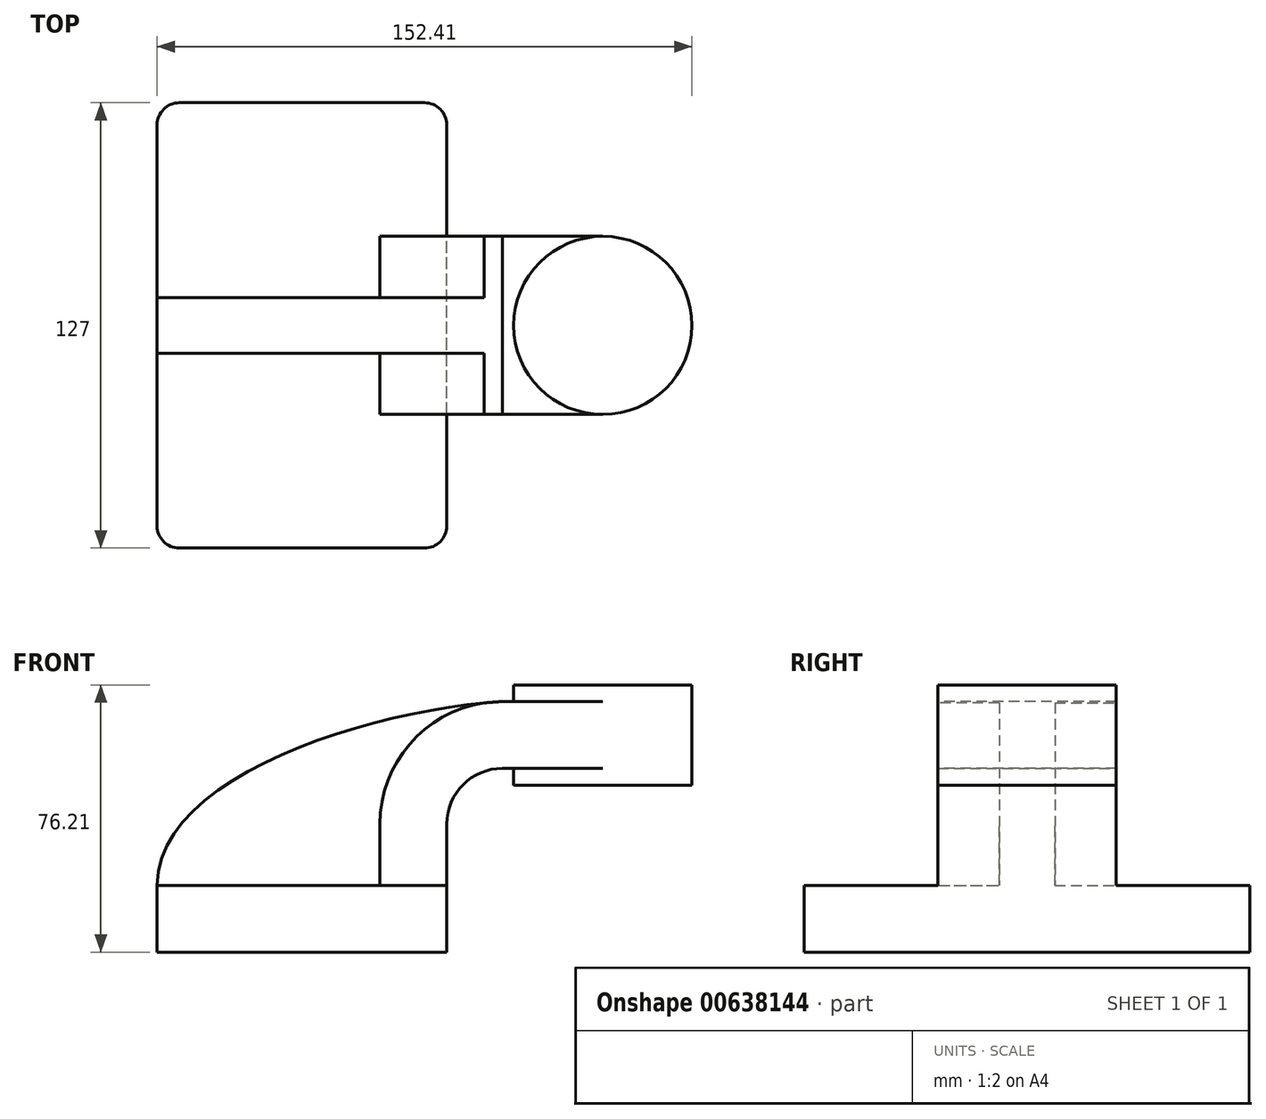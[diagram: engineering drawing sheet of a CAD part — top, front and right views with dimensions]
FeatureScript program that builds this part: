
annotation { "Feature Type Name" : "Feature", "Feature Type Description" : "" }
export const myFeature = defineFeature(function(context is Context, id is Id, definition is map)
    precondition{}
    {
        {
            var Q0;
            Q0=qCreatedBy(makeId("Front.planeOp"),FACE);
            var sketch = newSketch(context, id + "F0", { "sketchPlane" : qUnion([Q0])});
            skLineSegment(sketch, "E0.bottom", {"start": v(41.27, 9.53) * mm, "end": v(-41.28, 9.53) * mm});
            skLineSegment(sketch, "E0.top", {"start": v(41.28, -9.52) * mm, "end": v(-41.27, -9.52) * mm});
            skLineSegment(sketch, "E0.left", {"start": v(41.28, 9.53) * mm, "end": v(41.28, -9.52) * mm});
            skLineSegment(sketch, "E0.right", {"start": v(-41.28, 9.53) * mm, "end": v(-41.27, -9.52) * mm});
            skPoint(sketch, "E0.middle", {"position": v(0, 0) * mm});
            skLineSegment(sketch, "E1.bottom", {"start": v(60.32, 38.1) * mm, "end": v(111.12, 38.1) * mm});
            skLineSegment(sketch, "E1.top", {"start": v(60.32, 66.68) * mm, "end": v(111.12, 66.68) * mm});
            skLineSegment(sketch, "E1.left", {"start": v(60.32, 38.1) * mm, "end": v(60.32, 66.68) * mm});
            skLineSegment(sketch, "E1.right", {"start": v(111.12, 38.1) * mm, "end": v(111.12, 66.68) * mm});
            skPoint(sketch, "E1.middle", {"position": v(85.72, 52.39) * mm});
            skLineSegment(sketch, "E2", {"start": v(41.27, 9.53) * mm, "end": v(41.27, 27) * mm});
            skArc(sketch, "E3", {"start": v(41.27, 27) * mm, "mid": v(45.92, 38.23) * mm, "end": v(57.15, 42.88) * mm});
            skLineSegment(sketch, "E4", {"start": v(57.15, 42.88) * mm, "end": v(85.72, 42.88) * mm});
            skLineSegment(sketch, "E5.0", {"start": v(57.15, 61.93) * mm, "end": v(85.72, 61.93) * mm});
            skArc(sketch, "E5.1", {"start": v(22.23, 27) * mm, "mid": v(32.45, 51.7) * mm, "end": v(57.15, 61.93) * mm});
            skLineSegment(sketch, "E5.2", {"start": v(22.22, 9.53) * mm, "end": v(22.22, 27) * mm});
            skLineSegment(sketch, "E6", {"start": v(85.72, 66.68) * mm, "end": v(85.72, 38.1) * mm});
            skFitSpline(sketch, "E7", {"points": [v(57.15, 61.93) * mm, v(-41.28, 9.53) * mm], "startDerivative": vector(-107.61, -6.13) * mm, "endDerivative": vector(-0.12, -95.3) * mm});
            skSolve(sketch);
        }
        {
            var Q0;
            Q0=makeQuery(id+"F0.imprint","IMPRINT",FACE,{"disambiguationData":[TD([[makeQuery(id+"F0.imprint","IMPRINT",EDGE,{"derivedFrom":sQuery(id+"F0.wireOp",EDGE,"E0.top")}),-1.0]])]});
            extrude(context, id + "F1", {"entities" : qUnion([Q0]), "endBound" : BoundingType.SYMMETRIC, "depth" : 127 * mm, "offsetDistance" : 25.4 * mm});
        }
        {
            var Q0;
            {var subQ0=sQuery(id+"F0.wireOp",EDGE,"E4");var subQ1=sQuery(id+"F0.wireOp",EDGE,"E1.left");var subQ2=makeQuery(id+"F0.imprint","INTERSECT",VERTEX,{"derivedFrom":[subQ1,subQ0]});Q0=makeQuery(id+"F0.imprint","IMPRINT",FACE,{"disambiguationData":[TD([[makeQuery(id+"F0.imprint","IMPRINT",EDGE,{"disambiguationData":[TD([[subQ2,-1.0]])],"derivedFrom":subQ1}),-1.0]])]});}
            var Q1;
            {var subQ6=sQuery(id+"F0.wireOp",EDGE,"E2");Q1=makeQuery(id+"F0.imprint","IMPRINT",FACE,{"disambiguationData":[TD([[makeQuery(id+"F0.imprint","IMPRINT",EDGE,{"derivedFrom":subQ6}),1.0]])]});}
            extrude(context, id + "F2", {"entities" : qUnion([Q0, Q1]), "operationType" : NewBodyOperationType.ADD, "endBound" : BoundingType.SYMMETRIC, "depth" : 50.8 * mm, "offsetDistance" : 25.4 * mm});
        }
        {
            var Q0;
            {var subQ3=sQuery(id+"F0.wireOp",EDGE,"E5.2");Q0=makeQuery(id+"F0.imprint","IMPRINT",FACE,{"disambiguationData":[TD([[makeQuery(id+"F0.imprint","IMPRINT",EDGE,{"derivedFrom":subQ3}),1.0]])]});}
            extrude(context, id + "F3", {"entities" : qUnion([Q0]), "operationType" : NewBodyOperationType.ADD, "endBound" : BoundingType.SYMMETRIC, "depth" : 15.88 * mm, "offsetDistance" : 25.4 * mm});
        }
        {
            var Q0;
            {var subQ4=sQuery(id+"F0.wireOp",EDGE,"E1.right");Q0=makeQuery(id+"F0.imprint","IMPRINT",FACE,{"disambiguationData":[TD([[makeQuery(id+"F0.imprint","IMPRINT",EDGE,{"derivedFrom":subQ4}),1.0]])]});}
            var Q1;
            Q1=sQuery(id+"F0.wireOp",EDGE,"E6");
            revolve(context, id + "F4", {"operationType" : NewBodyOperationType.ADD, "entities" : qUnion([Q0]), "axis" : qUnion([Q1]), "revolveType" : RevolveType.FULL});
        }
        {
            var Q0;
            Q0=makeQuery(id+"F1.opExtrude","CAP_EDGE",EDGE,{"disambiguationData":[OSD([sQuery(id+"F0.wireOp",EDGE,"E0.left")])],"isStart":false});
            var Q1;
            Q1=makeQuery(id+"F1.opExtrude","CAP_EDGE",EDGE,{"disambiguationData":[OSD([sQuery(id+"F0.wireOp",EDGE,"E0.right")])],"isStart":false});
            var Q2;
            Q2=makeQuery(id+"F1.opExtrude","CAP_EDGE",EDGE,{"disambiguationData":[OSD([sQuery(id+"F0.wireOp",EDGE,"E0.right")])],"isStart":true});
            var Q3;
            Q3=makeQuery(id+"F1.opExtrude","CAP_EDGE",EDGE,{"disambiguationData":[OSD([sQuery(id+"F0.wireOp",EDGE,"E0.left")])],"isStart":true});
            fillet(context, id + "F5", {"entities" : qUnion([Q0, Q1, Q2, Q3]), "radius" : 6.35 * mm, "tangentPropagation" : true, "allowEdgeOverflow" : false});
        }
    });
